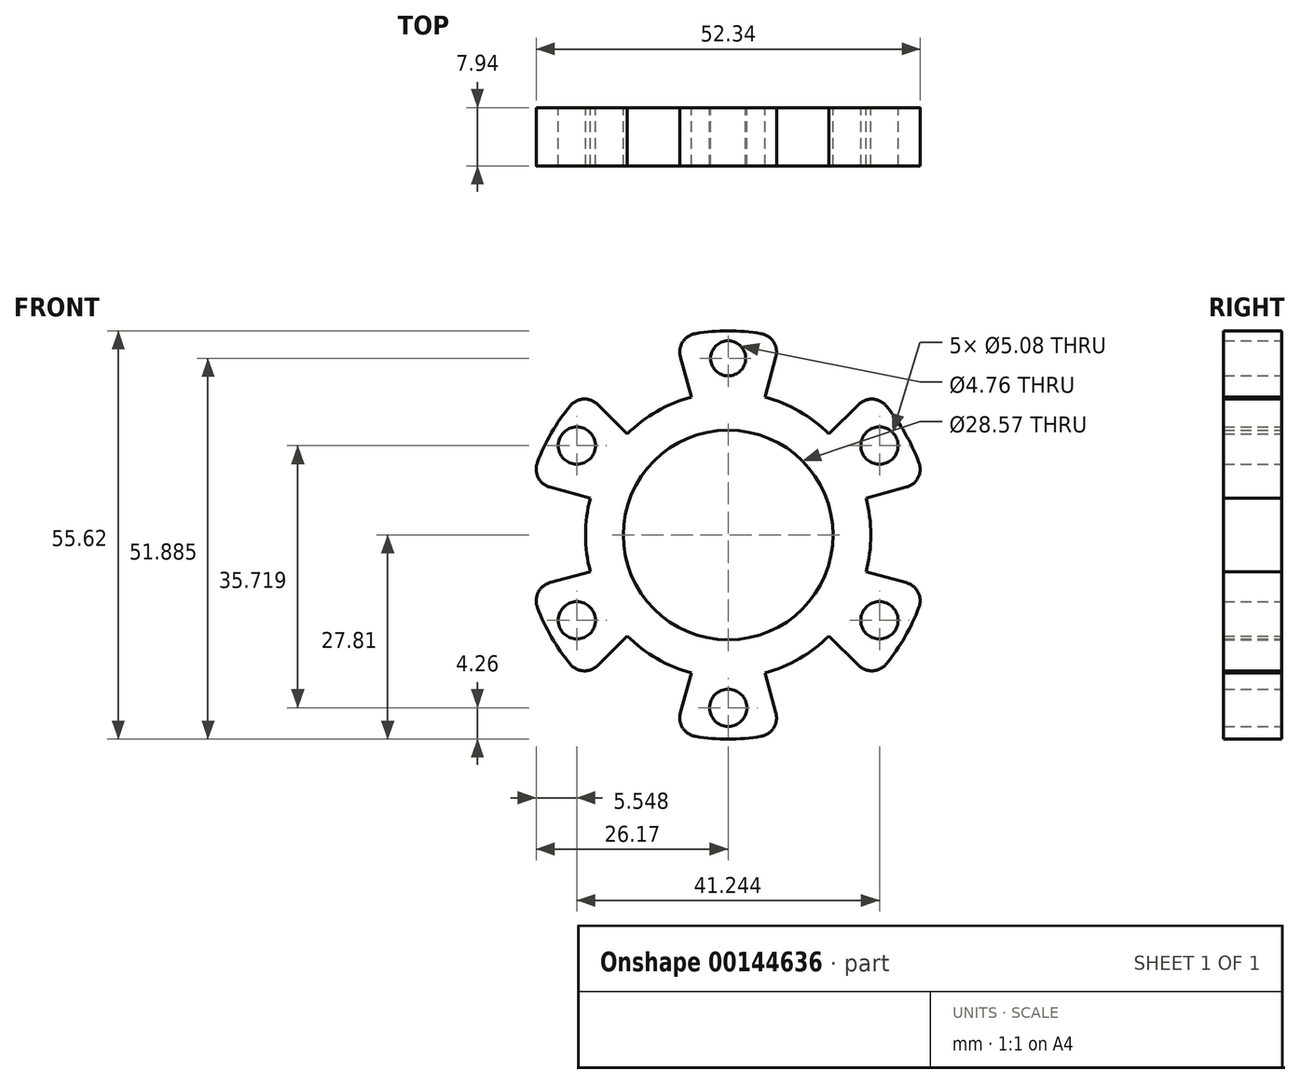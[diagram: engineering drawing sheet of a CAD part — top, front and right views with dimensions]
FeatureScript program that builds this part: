
annotation { "Feature Type Name" : "Feature", "Feature Type Description" : "" }
export const myFeature = defineFeature(function(context is Context, id is Id, definition is map)
    precondition{}
    {
        {
            var Q0;
            Q0=qCreatedBy(makeId("Front.planeOp"),FACE);
            var sketch = newSketch(context, id + "F0", { "sketchPlane" : qUnion([Q0])});
            skCircle(sketch, "E0", {"center": v(0, 24.08) * mm, "radius": 2.38 * mm});
            skCircle(sketch, "E1.1.0", {"center": v(-20.62, 12.17) * mm, "radius": 2.54 * mm});
            skCircle(sketch, "E1.2.0", {"center": v(-20.62, -11.64) * mm, "radius": 2.54 * mm});
            skCircle(sketch, "E1.3.0", {"center": v(0, -23.55) * mm, "radius": 2.54 * mm});
            skCircle(sketch, "E1.4.0", {"center": v(20.62, -11.64) * mm, "radius": 2.54 * mm});
            skCircle(sketch, "E1.5.0", {"center": v(20.62, 12.17) * mm, "radius": 2.54 * mm});
            skCircle(sketch, "E2", {"center": v(0, 0) * mm, "radius": 27.81 * mm});
            skCircle(sketch, "E3", {"center": v(0, 0) * mm, "radius": 19.45 * mm});
            skPoint(sketch, "E4", {"position": v(-18.78, 5.03) * mm});
            skPoint(sketch, "E5", {"position": v(-18.78, -5.03) * mm});
            skPoint(sketch, "E6", {"position": v(-26.87, 7.2) * mm});
            skPoint(sketch, "E7", {"position": v(-26.87, -7.2) * mm});
            skLineSegment(sketch, "E8", {"start": v(-18.78, 5.03) * mm, "end": v(-26.87, 7.2) * mm});
            skLineSegment(sketch, "E9", {"start": v(-18.78, -5.03) * mm, "end": v(-26.87, -7.2) * mm});
            skLineSegment(sketch, "E10.1.0", {"start": v(-5.03, -18.78) * mm, "end": v(-7.2, -26.87) * mm});
            skLineSegment(sketch, "E10.1.1", {"start": v(-13.75, -13.75) * mm, "end": v(-19.67, -19.67) * mm});
            skLineSegment(sketch, "E10.2.0", {"start": v(13.75, -13.75) * mm, "end": v(19.67, -19.67) * mm});
            skLineSegment(sketch, "E10.2.1", {"start": v(5.03, -18.78) * mm, "end": v(7.2, -26.87) * mm});
            skLineSegment(sketch, "E10.3.0", {"start": v(18.78, 5.03) * mm, "end": v(26.87, 7.2) * mm});
            skLineSegment(sketch, "E10.3.1", {"start": v(18.78, -5.03) * mm, "end": v(26.87, -7.2) * mm});
            skLineSegment(sketch, "E10.4.0", {"start": v(5.03, 18.78) * mm, "end": v(7.2, 26.87) * mm});
            skLineSegment(sketch, "E10.4.1", {"start": v(13.75, 13.75) * mm, "end": v(19.67, 19.67) * mm});
            skLineSegment(sketch, "E10.5.0", {"start": v(-13.75, 13.75) * mm, "end": v(-19.67, 19.67) * mm});
            skLineSegment(sketch, "E10.5.1", {"start": v(-5.03, 18.78) * mm, "end": v(-7.2, 26.87) * mm});
            skCircle(sketch, "E11", {"center": v(0, 0) * mm, "radius": 14.29 * mm});
            skSolve(sketch);
        }
        {
            var Q0;
            Q0=makeQuery(id+"F0.imprint","IMPRINT",FACE,{"disambiguationData":[TD([[makeQuery(id+"F0.imprint","IMPRINT",EDGE,{"derivedFrom":sQuery(id+"F0.wireOp",EDGE,"E1.1.0")}),-1.0]])]});
            var Q1;
            Q1=makeQuery(id+"F0.imprint","IMPRINT",FACE,{"disambiguationData":[TD([[makeQuery(id+"F0.imprint","IMPRINT",EDGE,{"derivedFrom":sQuery(id+"F0.wireOp",EDGE,"E0")}),-1.0]])]});
            var Q2;
            Q2=makeQuery(id+"F0.imprint","IMPRINT",FACE,{"disambiguationData":[TD([[makeQuery(id+"F0.imprint","IMPRINT",EDGE,{"derivedFrom":sQuery(id+"F0.wireOp",EDGE,"E1.5.0")}),-1.0]])]});
            var Q3;
            Q3=makeQuery(id+"F0.imprint","IMPRINT",FACE,{"disambiguationData":[TD([[makeQuery(id+"F0.imprint","IMPRINT",EDGE,{"derivedFrom":sQuery(id+"F0.wireOp",EDGE,"E1.4.0")}),-1.0]])]});
            var Q4;
            Q4=makeQuery(id+"F0.imprint","IMPRINT",FACE,{"disambiguationData":[TD([[makeQuery(id+"F0.imprint","IMPRINT",EDGE,{"derivedFrom":sQuery(id+"F0.wireOp",EDGE,"E1.3.0")}),-1.0]])]});
            var Q5;
            Q5=makeQuery(id+"F0.imprint","IMPRINT",FACE,{"disambiguationData":[TD([[makeQuery(id+"F0.imprint","IMPRINT",EDGE,{"derivedFrom":sQuery(id+"F0.wireOp",EDGE,"E1.2.0")}),-1.0]])]});
            var Q6;
            Q6=makeQuery(id+"F0.imprint","IMPRINT",FACE,{"disambiguationData":[TD([[makeQuery(id+"F0.imprint","IMPRINT",EDGE,{"derivedFrom":sQuery(id+"F0.wireOp",EDGE,"E11")}),-1.0]])]});
            extrude(context, id + "F1", {"entities" : qUnion([Q0, Q1, Q2, Q3, Q4, Q5, Q6]), "depth" : 7.94 * mm});
        }
        {
            var Q0;
            Q0=makeQuery(id+"F1.opExtrude","SWEPT_EDGE",EDGE,{"disambiguationData":[OSD([sQuery(id+"F0.wireOp",EDGE,"E2"),sQuery(id+"F0.wireOp",EDGE,"E8")])]});
            var Q1;
            Q1=makeQuery(id+"F1.opExtrude","SWEPT_EDGE",EDGE,{"disambiguationData":[OSD([sQuery(id+"F0.wireOp",EDGE,"E2"),sQuery(id+"F0.wireOp",EDGE,"E9")])]});
            var Q2;
            Q2=makeQuery(id+"F1.opExtrude","SWEPT_EDGE",EDGE,{"disambiguationData":[OSD([sQuery(id+"F0.wireOp",EDGE,"E2"),sQuery(id+"F0.wireOp",EDGE,"E10.1.1")])]});
            var Q3;
            Q3=makeQuery(id+"F1.opExtrude","SWEPT_EDGE",EDGE,{"disambiguationData":[OSD([sQuery(id+"F0.wireOp",EDGE,"E2"),sQuery(id+"F0.wireOp",EDGE,"E10.1.0")])]});
            var Q4;
            Q4=makeQuery(id+"F1.opExtrude","SWEPT_EDGE",EDGE,{"disambiguationData":[OSD([sQuery(id+"F0.wireOp",EDGE,"E2"),sQuery(id+"F0.wireOp",EDGE,"E10.2.1")])]});
            var Q5;
            Q5=makeQuery(id+"F1.opExtrude","SWEPT_EDGE",EDGE,{"disambiguationData":[OSD([sQuery(id+"F0.wireOp",EDGE,"E2"),sQuery(id+"F0.wireOp",EDGE,"E10.2.0")])]});
            var Q6;
            Q6=makeQuery(id+"F1.opExtrude","SWEPT_EDGE",EDGE,{"disambiguationData":[OSD([sQuery(id+"F0.wireOp",EDGE,"E2"),sQuery(id+"F0.wireOp",EDGE,"E10.3.1")])]});
            var Q7;
            Q7=makeQuery(id+"F1.opExtrude","SWEPT_EDGE",EDGE,{"disambiguationData":[OSD([sQuery(id+"F0.wireOp",EDGE,"E2"),sQuery(id+"F0.wireOp",EDGE,"E10.3.0")])]});
            var Q8;
            Q8=makeQuery(id+"F1.opExtrude","SWEPT_EDGE",EDGE,{"disambiguationData":[OSD([sQuery(id+"F0.wireOp",EDGE,"E2"),sQuery(id+"F0.wireOp",EDGE,"E10.4.1")])]});
            var Q9;
            Q9=makeQuery(id+"F1.opExtrude","SWEPT_EDGE",EDGE,{"disambiguationData":[OSD([sQuery(id+"F0.wireOp",EDGE,"E2"),sQuery(id+"F0.wireOp",EDGE,"E10.4.0")])]});
            var Q10;
            Q10=makeQuery(id+"F1.opExtrude","SWEPT_EDGE",EDGE,{"disambiguationData":[OSD([sQuery(id+"F0.wireOp",EDGE,"E2"),sQuery(id+"F0.wireOp",EDGE,"E10.5.1")])]});
            var Q11;
            Q11=makeQuery(id+"F1.opExtrude","SWEPT_EDGE",EDGE,{"disambiguationData":[OSD([sQuery(id+"F0.wireOp",EDGE,"E2"),sQuery(id+"F0.wireOp",EDGE,"E10.5.0")])]});
            fillet(context, id + "F2", {"entities" : qUnion([Q0, Q1, Q2, Q3, Q4, Q5, Q6, Q7, Q8, Q9, Q10, Q11]), "radius" : 2.54 * mm, "tangentPropagation" : true, "defaultsChanged" : true, "vertexSettings" : [], "allowEdgeOverflow" : false});
        }
    });
